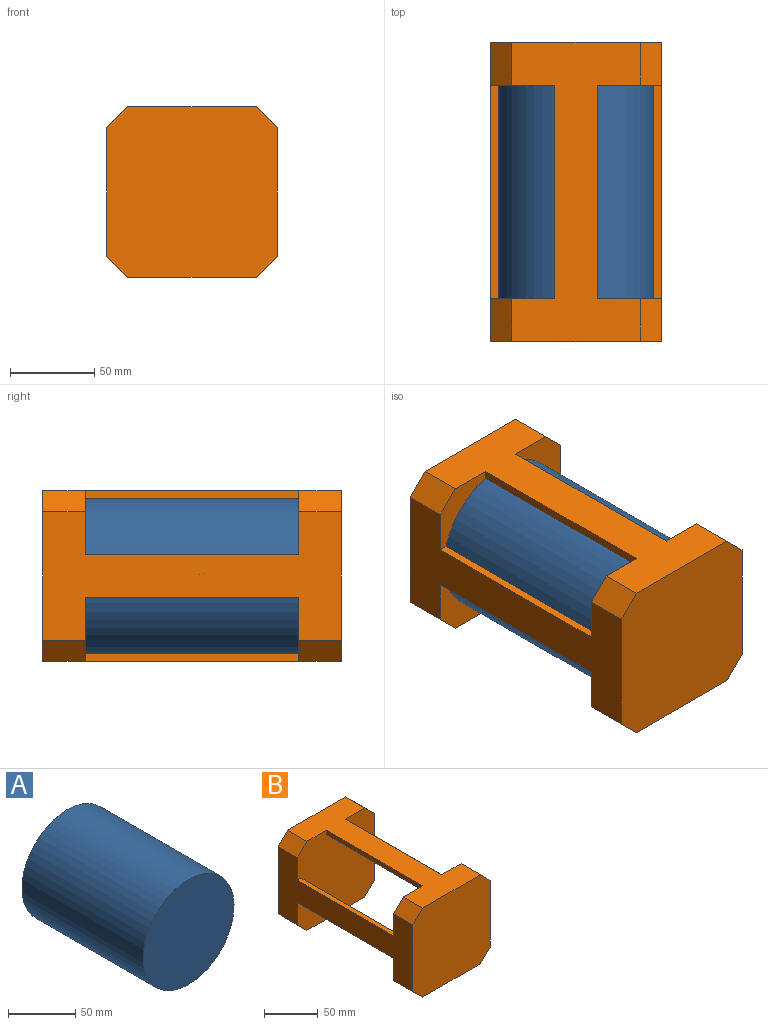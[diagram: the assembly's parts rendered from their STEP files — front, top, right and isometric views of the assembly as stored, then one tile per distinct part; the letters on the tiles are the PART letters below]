
ASSEMBLY  parts=2 mates=1
PART A: 3 faces, bbox 95.3x127x95.3 mm
  f0: cylinder r=47.62mm len=127mm, axis (0,-1,0), area 38003.1mm2, adj f1,f2
  f1: plane 95.25x95.25mm, normal (0,1,0), area 7125.6mm2, adj f0
  f2: plane 95.25x95.25mm, normal (0,-1,0), area 7125.6mm2, adj f0
PART B: 28 faces, bbox 101.6x177.8x101.6 mm
  f0: plane 101.6x101.6mm, normal (0,1,0), area 9619.4mm2, adj f1,f2,f3,f4,f5,f6,f7,f8
  f1: plane 177.8x76.2mm, normal (0,0,-1), area 7096.8mm2, adj f0,f2,f8,f9,f13,f14,f22,f23
  f2: plane 25.4x12.7mm, normal (0.71,0,-0.71), area 456.2mm2, adj f0,f1,f3,f9
  f3: plane 177.8x76.2mm, normal (1,0,0), area 7096.8mm2, adj f0,f2,f4,f9,f19,f21,f22,f23
  f4: plane 25.4x12.7mm, normal (0.71,0,0.71), area 456.2mm2, adj f0,f3,f5,f9
  f5: plane 177.8x76.2mm, normal (0,0,1), area 7096.8mm2, adj f0,f4,f6,f9,f10,f12,f22,f24
  f6: plane 25.4x12.7mm, normal (-0.71,0,0.71), area 456.2mm2, adj f0,f5,f7,f9
  f7: plane 177.8x76.2mm, normal (-1,0,0), area 7096.8mm2, adj f0,f6,f8,f9,f17,f18,f22,f25
  f8: plane 25.4x12.7mm, normal (-0.71,0,-0.71), area 456.2mm2, adj f0,f1,f7,f9
  f9: plane 101.6x101.6mm, normal (0,-1,0), area 10000mm2, adj f1,f2,f3,f4,f5,f6,f7,f8
  f10: plane 127x4.9mm, normal (-1,0,0), area 622.2mm2, adj f0,f5,f11,f22
  f11: cylinder r=47.62mm len=127mm, axis (0,-1,0), area 3265.3mm2, adj f0,f10,f12,f22
  f12: plane 127x4.9mm, normal (1,0,0), area 622.2mm2, adj f0,f5,f11,f22
  f13: plane 127x4.9mm, normal (-1,0,0), area 622.2mm2, adj f0,f1,f15,f22
  f14: plane 127x4.9mm, normal (1,0,0), area 622.2mm2, adj f0,f1,f15,f22
  f15: cylinder r=47.62mm len=127mm, axis (0,-1,0), area 3265.3mm2, adj f0,f13,f14,f22
  f16: cylinder r=47.62mm len=127mm, axis (0,-1,0), area 3265.3mm2, adj f0,f17,f18,f22
  f17: plane 127x4.9mm, normal (0,0,1), area 622.2mm2, adj f0,f7,f16,f22
  f18: plane 127x4.9mm, normal (0,0,-1), area 622.2mm2, adj f0,f7,f16,f22
  f19: plane 127x4.9mm, normal (0,0,1), area 622.2mm2, adj f0,f3,f20,f22
  f20: cylinder r=47.62mm len=127mm, axis (0,-1,0), area 3265.3mm2, adj f0,f19,f21,f22
  f21: plane 127x4.9mm, normal (0,0,-1), area 622.2mm2, adj f0,f3,f20,f22
  f22: plane 101.6x101.6mm, normal (0,-1,0), area 9619.4mm2, adj f1,f3,f5,f7,f10,f11,f12,f13
  f23: plane 25.4x12.7mm, normal (0.71,0,-0.71), area 456.2mm2, adj f1,f3,f22,f27
  f24: plane 25.4x12.7mm, normal (0.71,0,0.71), area 456.2mm2, adj f3,f5,f22,f27
  f25: plane 25.4x12.7mm, normal (-0.71,0,0.71), area 456.2mm2, adj f5,f7,f22,f27
  f26: plane 25.4x12.7mm, normal (-0.71,0,-0.71), area 456.2mm2, adj f1,f7,f22,f27
  f27: plane 101.6x101.6mm, normal (0,1,0), area 10000mm2, adj f1,f3,f5,f7,f23,f24,f25,f26
PLACE A t=(466.94,-64.22,-0.72)mm
PLACE B t=(-0.42,-64.22,-0.72)mm
MATE fastened A.f0 <-> B.f20  axis (0,-1,0) through (-0.42,62.78,-0.72)mm
